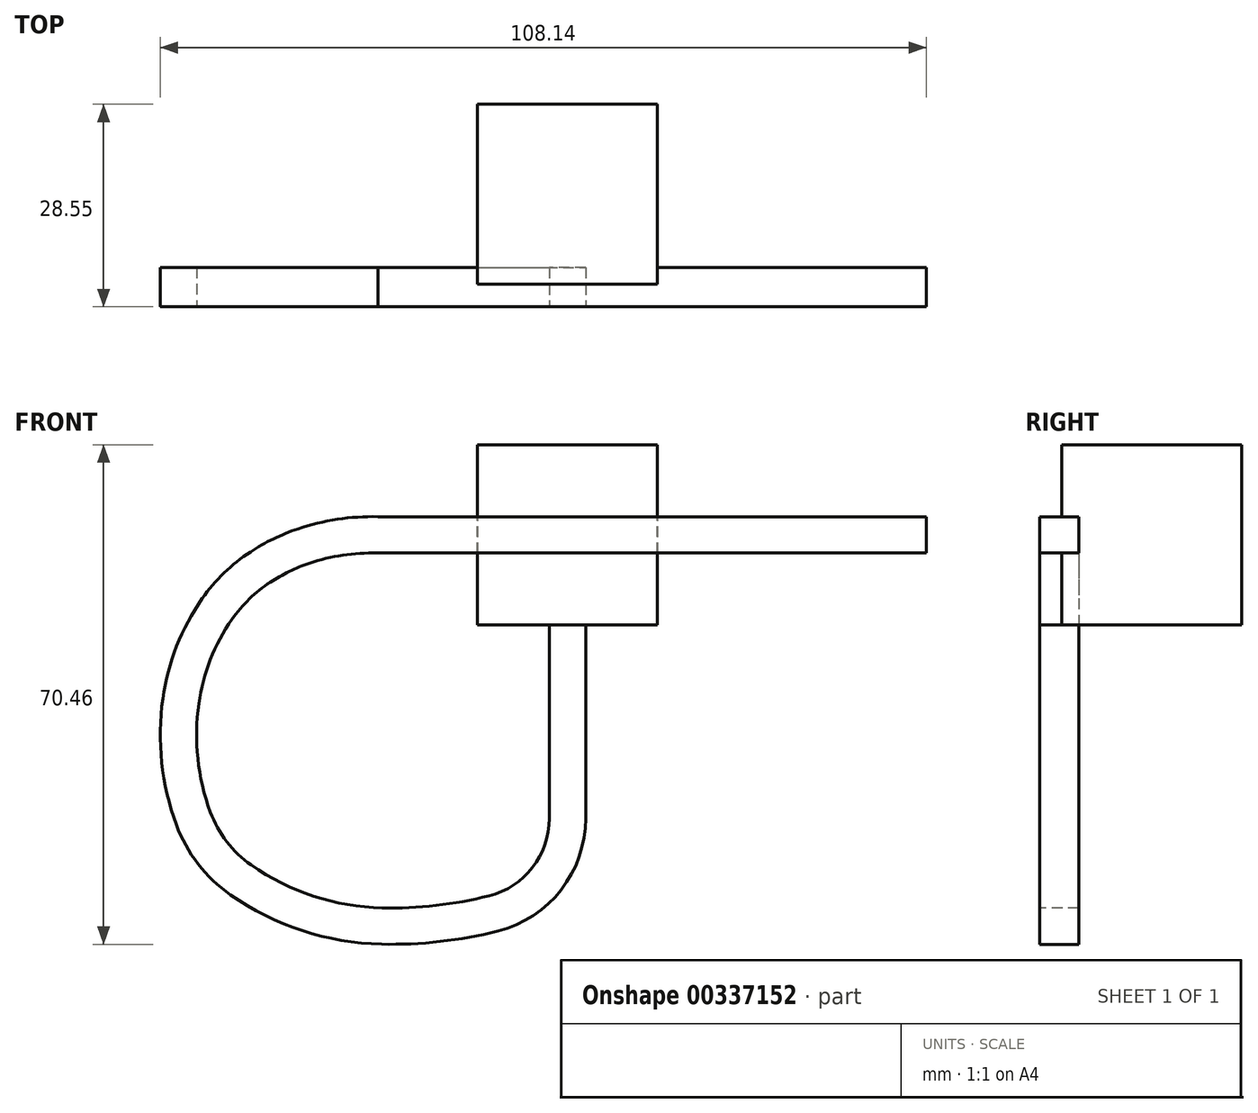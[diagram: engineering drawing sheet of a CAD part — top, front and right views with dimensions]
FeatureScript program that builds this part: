
annotation { "Feature Type Name" : "Feature", "Feature Type Description" : "" }
export const myFeature = defineFeature(function(context is Context, id is Id, definition is map)
    precondition{}
    {
        {
            var Q0;
            Q0=qCreatedBy(makeId("Front.planeOp"),FACE);
            var sketch = newSketch(context, id + "F0", { "sketchPlane" : qUnion([Q0])});
            skLineSegment(sketch, "E0.bottom", {"start": v(12.7, 12.7) * mm, "end": v(-12.7, 12.7) * mm});
            skLineSegment(sketch, "E0.top", {"start": v(12.7, -12.7) * mm, "end": v(-12.7, -12.7) * mm});
            skLineSegment(sketch, "E0.left", {"start": v(12.7, 12.7) * mm, "end": v(12.7, -12.7) * mm});
            skLineSegment(sketch, "E0.right", {"start": v(-12.7, 12.7) * mm, "end": v(-12.7, -12.7) * mm});
            skPoint(sketch, "E0.middle", {"position": v(0, 0) * mm});
            skSolve(sketch);
        }
        {
            var Q0;
            Q0=makeQuery(id+"F0.imprint","IMPRINT",FACE,{"disambiguationData":[TD([[makeQuery(id+"F0.imprint","IMPRINT",EDGE,{"derivedFrom":sQuery(id+"F0.wireOp",EDGE,"E0.bottom")}),1.0]])]});
            extrude(context, id + "F1", {"entities" : qUnion([Q0]), "depth" : 25.4 * mm, "symmetric" : true});
        }
        {
            var Q0;
            Q0=makeQuery(id+"F1.opExtrude","CAP_FACE",FACE,{"disambiguationData":[OSD([sQuery(id+"F0.wireOp",EDGE,"E0.bottom"),sQuery(id+"F0.wireOp",EDGE,"E0.top"),sQuery(id+"F0.wireOp",EDGE,"E0.left"),sQuery(id+"F0.wireOp",EDGE,"E0.right")])],"isStart":false});
            var sketch = newSketch(context, id + "F2", { "sketchPlane" : qUnion([Q0])});
            skLineSegment(sketch, "E1", {"start": v(0, -12.7) * mm, "end": v(0, -40) * mm});
            skPoint(sketch, "E1.endSnap0", {"position": v(0, -12.7) * mm});
            skArc(sketch, "E2", {"start": v(0, -40) * mm, "mid": v(-2.92, -48.5) * mm, "end": v(-10.44, -53.4) * mm});
            skArc(sketch, "E3", {"start": v(-10.44, -53.4) * mm, "mid": v(-18.27, -54.82) * mm, "end": v(-26.21, -55.18) * mm});
            skArc(sketch, "E4", {"start": v(-26.21, -55.18) * mm, "mid": v(-36.64, -53.4) * mm, "end": v(-46.11, -48.68) * mm});
            skArc(sketch, "E5", {"start": v(-46.11, -48.68) * mm, "mid": v(-50.13, -44.85) * mm, "end": v(-52.81, -40) * mm});
            skArc(sketch, "E6", {"start": v(-52.81, -40) * mm, "mid": v(-54.73, -31.84) * mm, "end": v(-54.59, -23.45) * mm});
            skArc(sketch, "E7", {"start": v(-54.59, -23.45) * mm, "mid": v(-52.8, -16.65) * mm, "end": v(-49.46, -10.44) * mm});
            skArc(sketch, "E8", {"start": v(-49.46, -10.44) * mm, "mid": v(-46.7, -7.2) * mm, "end": v(-43.36, -4.53) * mm});
            skArc(sketch, "E9", {"start": v(-43.36, -4.53) * mm, "mid": v(-40.4, -2.86) * mm, "end": v(-37.25, -1.58) * mm});
            skArc(sketch, "E10", {"start": v(-37.25, -1.58) * mm, "mid": v(-32.1, -0.33) * mm, "end": v(-26.8, 0) * mm});
            skLineSegment(sketch, "E11", {"start": v(-26.8, 0) * mm, "end": v(50.65, 0) * mm});
            skPoint(sketch, "E11.endSnap0", {"position": v(-12.7, 0) * mm});
            skSolve(sketch);
        }
        {
            var Q0;
            Q0=sQuery(id+"F2.wireOp",VERTEX,"E11.end");
            var Q1;
            Q1=qCreatedBy(makeId("Right.planeOp"),FACE);
            cPlane(context, id + "F3", {"entities" : qUnion([Q0, Q1]), "cplaneType" : CPlaneType.PLANE_POINT, "offset" : 25.4 * mm, "width" : 152.4 * mm, "height" : 152.4 * mm});
        }
        {
            var Q0;
            Q0=qCreatedBy(id+"F3.planeOp",FACE);
            var sketch = newSketch(context, id + "F4", { "sketchPlane" : qUnion([Q0])});
            skLineSegment(sketch, "E12.bottom", {"start": v(-10.34, 2.56) * mm, "end": v(-15.85, 2.56) * mm});
            skLineSegment(sketch, "E12.top", {"start": v(-10.34, -2.56) * mm, "end": v(-15.85, -2.56) * mm});
            skLineSegment(sketch, "E12.left", {"start": v(-10.34, 2.56) * mm, "end": v(-10.34, -2.56) * mm});
            skLineSegment(sketch, "E12.right", {"start": v(-15.85, 2.56) * mm, "end": v(-15.85, -2.56) * mm});
            skPoint(sketch, "E12.middle", {"position": v(-13.1, 0) * mm});
            skSolve(sketch);
        }
        {
            var Q0;
            Q0=makeQuery(id+"F4.imprint","IMPRINT",FACE,{"disambiguationData":[TD([[makeQuery(id+"F4.imprint","IMPRINT",EDGE,{"derivedFrom":sQuery(id+"F4.wireOp",EDGE,"E12.bottom")}),1.0]])]});
            var Q1;
            Q1 = qConstructionFilter(qBodyType(qCreatedBy(id + "F2" ,EDGE), BodyType.WIRE), ConstructionObject.NO);
            sweep(context, id + "F5", {"operationType" : NewBodyOperationType.ADD, "profiles" : qUnion([Q0]), "path" : qUnion([Q1])});
        }
    });
